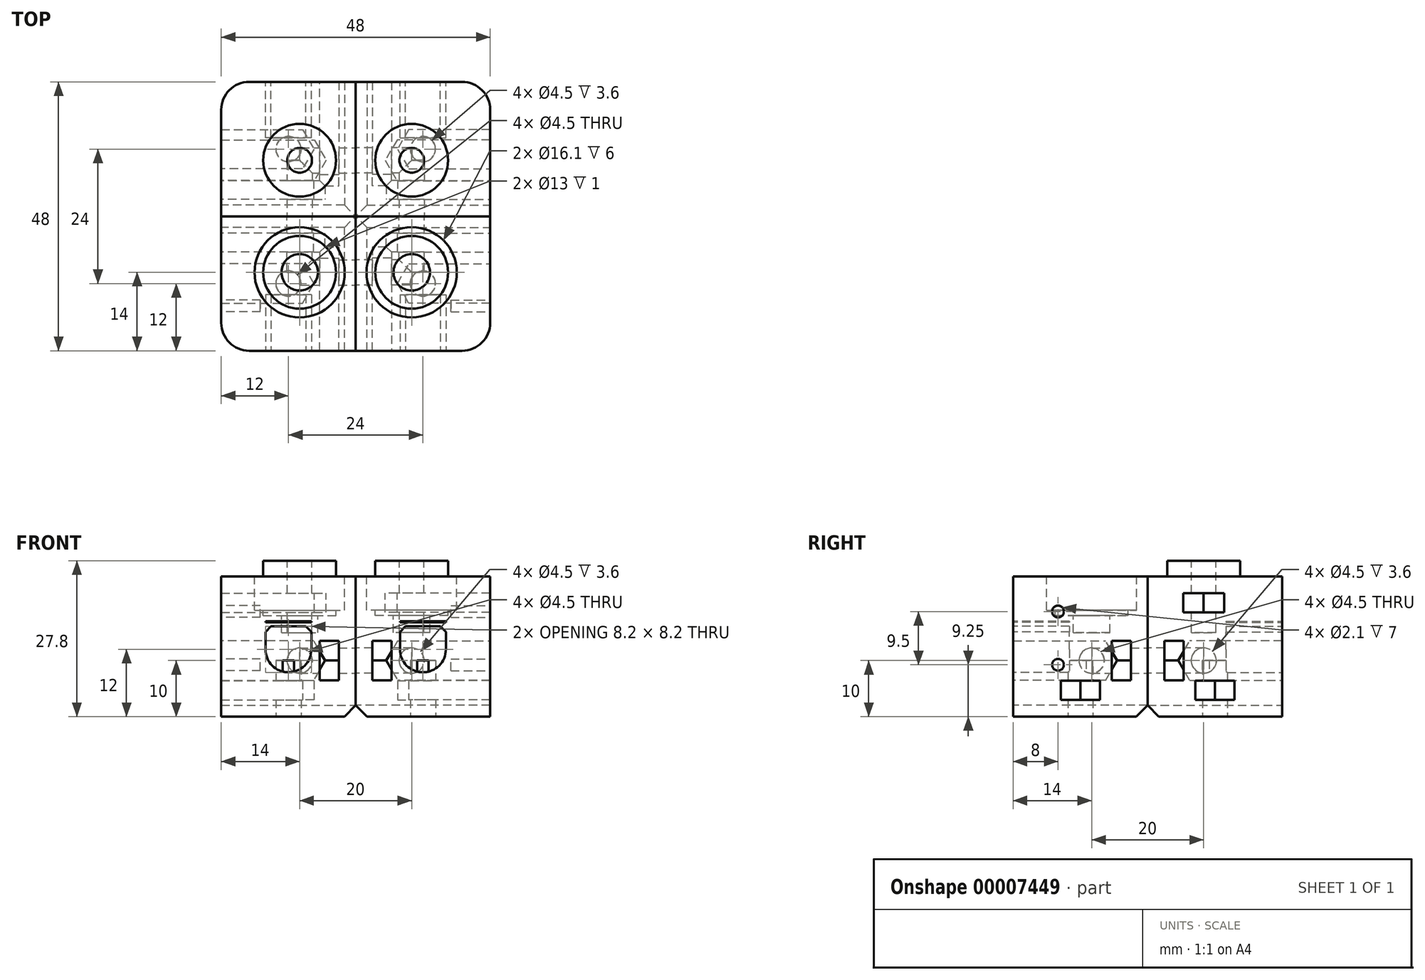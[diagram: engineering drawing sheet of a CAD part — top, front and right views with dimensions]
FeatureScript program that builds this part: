
annotation { "Feature Type Name" : "Feature", "Feature Type Description" : "" }
export const myFeature = defineFeature(function(context is Context, id is Id, definition is map)
    precondition{}
    {
        {
            var Q0;
            Q0=qCreatedBy(makeId("Top.planeOp"),FACE);
            var sketch = newSketch(context, id + "F0", { "sketchPlane" : qUnion([Q0])});
            skLineSegment(sketch, "E0.bottom", {"start": v(0, 0) * mm, "end": v(24, 0) * mm});
            skLineSegment(sketch, "E0.top", {"start": v(0, -24) * mm, "end": v(24, -24) * mm});
            skLineSegment(sketch, "E0.left", {"start": v(0, 0) * mm, "end": v(0, -24) * mm});
            skLineSegment(sketch, "E0.right", {"start": v(24, 0) * mm, "end": v(24, -24) * mm});
            skCircle(sketch, "E1", {"center": v(12, -12) * mm, "radius": 2.25 * mm});
            skLineSegment(sketch, "E2.3", {"start": v(9.48, -15.5) * mm, "end": v(7.46, -12) * mm});
            skLineSegment(sketch, "E2.4", {"start": v(7.46, -12) * mm, "end": v(9.48, -8.5) * mm});
            skLineSegment(sketch, "E3", {"start": v(24, -8.5) * mm, "end": v(24, -15.5) * mm});
            skLineSegment(sketch, "E4", {"start": v(9.48, -8.5) * mm, "end": v(24, -8.5) * mm});
            skLineSegment(sketch, "E5", {"start": v(24, -15.5) * mm, "end": v(9.48, -15.5) * mm});
            skLineSegment(sketch, "E6", {"start": v(8.47, -13.75) * mm, "end": v(11.5, -12) * mm, "construction": true});
            skLineSegment(sketch, "E7", {"start": v(11.5, -12) * mm, "end": v(12, -12) * mm, "construction": true});
            skLineSegment(sketch, "E8", {"start": v(7.46, -12) * mm, "end": v(11.5, -12) * mm, "construction": true});
            skSolve(sketch);
        }
        {
            var Q0;
            Q0 = qSketchRegion(id + "F0", true);
            var Q1;
            Q1=makeQuery(id+"F0.imprint","IMPRINT",FACE,{"disambiguationData":[TD([[makeQuery(id+"F0.imprint","IMPRINT",EDGE,{"derivedFrom":sQuery(id+"F0.wireOp",EDGE,"E1")}),-1.0]])]});
            var Q2;
            Q2=makeQuery(id+"F0.imprint","IMPRINT",FACE,{"disambiguationData":[TD([[makeQuery(id+"F0.imprint","IMPRINT",EDGE,{"derivedFrom":sQuery(id+"F0.wireOp",EDGE,"E1")}),1.0]])]});
            extrude(context, id + "F1", {"entities" : qUnion([Q0, Q1, Q2]), "depth" : 25 * mm});
        }
        {
            var Q0;
            Q0=makeQuery(id+"F0.imprint","IMPRINT",FACE,{"disambiguationData":[TD([[makeQuery(id+"F0.imprint","IMPRINT",EDGE,{"derivedFrom":sQuery(id+"F0.wireOp",EDGE,"E1")}),1.0]])]});
            extrude(context, id + "F2", {"entities" : qUnion([Q0]), "operationType" : NewBodyOperationType.REMOVE, "depth" : 10 * mm});
        }
        {
            var Q0;
            Q0=makeQuery(id+"F0.imprint","IMPRINT",FACE,{"disambiguationData":[TD([[makeQuery(id+"F0.imprint","IMPRINT",EDGE,{"derivedFrom":sQuery(id+"F0.wireOp",EDGE,"E2.0")}),1.0]])]});
            var Q1;
            Q1=makeQuery(id+"F0.imprint","IMPRINT",FACE,{"disambiguationData":[TD([[makeQuery(id+"F0.imprint","IMPRINT",EDGE,{"derivedFrom":sQuery(id+"F0.wireOp",EDGE,"E1")}),-1.0]])]});
            extrude(context, id + "F3", {"entities" : qUnion([Q0, Q1]), "operationType" : NewBodyOperationType.REMOVE, "depth" : 3 * mm + 3.4 * mm});
        }
        {
            var Q0;
            Q0=makeQuery(id+"F0.imprint","IMPRINT",FACE,{"disambiguationData":[TD([[makeQuery(id+"F0.imprint","IMPRINT",EDGE,{"derivedFrom":sQuery(id+"F0.wireOp",EDGE,"E1")}),-1.0]])]});
            var Q1;
            Q1=makeQuery(id+"F0.imprint","IMPRINT",FACE,{"disambiguationData":[TD([[makeQuery(id+"F0.imprint","IMPRINT",EDGE,{"derivedFrom":sQuery(id+"F0.wireOp",EDGE,"E2.0")}),1.0]])]});
            extrude(context, id + "F4", {"entities" : qUnion([Q0, Q1]), "operationType" : NewBodyOperationType.ADD, "depth" : 3 * mm});
        }
        {
            var Q0;
            Q0=makeQuery(id+"F1.opExtrude","SWEPT_FACE",FACE,{"disambiguationData":[OSD([sQuery(id+"F0.wireOp",EDGE,"E0.top")])]});
            var sketch = newSketch(context, id + "F5", { "sketchPlane" : qUnion([Q0])});
            skCircle(sketch, "E9", {"center": v(12, 12) * mm, "radius": 4 * mm});
            skLineSegment(sketch, "E10", {"start": v(8.72, 14.3) * mm, "end": v(10.76, 17.2) * mm});
            skLineSegment(sketch, "E11", {"start": v(10.76, 17.2) * mm, "end": v(13.24, 17.2) * mm});
            skLineSegment(sketch, "E12", {"start": v(13.24, 17.2) * mm, "end": v(15.28, 14.3) * mm});
            skSolve(sketch);
        }
        {
            var Q0;
            {var subQ1=sQuery(id+"F5.wireOp",EDGE,"E10");Q0=makeQuery(id+"F5.imprint","IMPRINT",FACE,{"disambiguationData":[TD([[makeQuery(id+"F5.imprint","IMPRINT",EDGE,{"derivedFrom":subQ1}),1.0]])]});}
            var sketch = newSketch(context, id + "F6", { "sketchPlane" : qUnion([Q0])});
            skCircle(sketch, "E13", {"center": v(12, 12) * mm, "radius": 4.1 * mm});
            skLineSegment(sketch, "E14", {"start": v(16.1, 12) * mm, "end": v(16.1, 16.1) * mm, "construction": true});
            skLineSegment(sketch, "E15", {"start": v(16.1, 16.1) * mm, "end": v(7.9, 16.1) * mm});
            skLineSegment(sketch, "E16", {"start": v(7.9, 16.1) * mm, "end": v(7.9, 12) * mm, "construction": true});
            skLineSegment(sketch, "E17", {"start": v(7.9, 16.1) * mm, "end": v(7.9, 17) * mm, "construction": true});
            skLineSegment(sketch, "E18", {"start": v(7.9, 17) * mm, "end": v(7.9, 16.8) * mm});
            skLineSegment(sketch, "E19", {"start": v(7.9, 16.8) * mm, "end": v(16.1, 16.8) * mm});
            skLineSegment(sketch, "E20", {"start": v(16.1, 16.8) * mm, "end": v(16.1, 17) * mm});
            skLineSegment(sketch, "E21", {"start": v(16.1, 17) * mm, "end": v(7.9, 17) * mm});
            skLineSegment(sketch, "E22", {"start": v(15.1, 16.1) * mm, "end": v(16.1, 15.1) * mm});
            skLineSegment(sketch, "E23", {"start": v(16.1, 15.1) * mm, "end": v(16.1, 12) * mm});
            skLineSegment(sketch, "E24", {"start": v(7.9, 12) * mm, "end": v(7.9, 15.1) * mm});
            skLineSegment(sketch, "E25", {"start": v(7.9, 15.1) * mm, "end": v(8.9, 16.1) * mm});
            skSolve(sketch);
        }
        {
            var Q0;
            Q0 = qSketchRegion(id + "F6", true);
            extrude(context, id + "F7", {"entities" : qUnion([Q0]), "operationType" : NewBodyOperationType.REMOVE, "oppositeDirection" : true, "depth" : 10 * mm});
        }
        {
            var Q0;
            Q0=makeQuery(id+"F1.opExtrude","SWEPT_FACE",FACE,{"disambiguationData":[OSD([sQuery(id+"F0.wireOp",EDGE,"E0.left")])]});
            var sketch = newSketch(context, id + "F8", { "sketchPlane" : qUnion([Q0])});
            skCircle(sketch, "E26", {"center": v(10, 10) * mm, "radius": 2.25 * mm});
            skLineSegment(sketch, "E27.3", {"start": v(7.48, 6.5) * mm, "end": v(5.46, 10) * mm});
            skLineSegment(sketch, "E27.4", {"start": v(5.46, 10) * mm, "end": v(7.48, 13.5) * mm});
            skLineSegment(sketch, "E28", {"start": v(24, 6.5) * mm, "end": v(24, 13.5) * mm});
            skLineSegment(sketch, "E29", {"start": v(24, 13.5) * mm, "end": v(7.48, 13.5) * mm});
            skLineSegment(sketch, "E30", {"start": v(7.48, 6.5) * mm, "end": v(24, 6.5) * mm});
            skLineSegment(sketch, "E31", {"start": v(10, 13.5) * mm, "end": v(10, 6.5) * mm, "construction": true});
            skLineSegment(sketch, "E32", {"start": v(6.47, 11.75) * mm, "end": v(9.5, 10) * mm, "construction": true});
            skLineSegment(sketch, "E33", {"start": v(9.5, 10) * mm, "end": v(10, 10) * mm, "construction": true});
            skSolve(sketch);
        }
        {
            var Q0;
            Q0=makeQuery(id+"F8.imprint","IMPRINT",FACE,{"disambiguationData":[TD([[makeQuery(id+"F8.imprint","IMPRINT",EDGE,{"derivedFrom":sQuery(id+"F8.wireOp",EDGE,"E26")}),1.0]])]});
            extrude(context, id + "F9", {"entities" : qUnion([Q0]), "operationType" : NewBodyOperationType.REMOVE, "oppositeDirection" : true, "depth" : 10 * mm});
        }
        {
            var Q0;
            Q0=makeQuery(id+"F8.imprint","IMPRINT",FACE,{"disambiguationData":[TD([[makeQuery(id+"F8.imprint","IMPRINT",EDGE,{"derivedFrom":sQuery(id+"F8.wireOp",EDGE,"E26")}),-1.0]])]});
            var Q1;
            Q1=makeQuery(id+"F8.imprint","IMPRINT",FACE,{"disambiguationData":[TD([[makeQuery(id+"F8.imprint","IMPRINT",EDGE,{"derivedFrom":sQuery(id+"F8.wireOp",EDGE,"E27.0")}),1.0]])]});
            extrude(context, id + "F10", {"entities" : qUnion([Q0, Q1]), "operationType" : NewBodyOperationType.REMOVE, "oppositeDirection" : true, "depth" : 3 * mm + 3.4 * mm});
        }
        {
            var Q0;
            Q0=makeQuery(id+"F8.imprint","IMPRINT",FACE,{"disambiguationData":[TD([[makeQuery(id+"F8.imprint","IMPRINT",EDGE,{"derivedFrom":sQuery(id+"F8.wireOp",EDGE,"E26")}),-1.0]])]});
            var Q1;
            Q1=makeQuery(id+"F8.imprint","IMPRINT",FACE,{"disambiguationData":[TD([[makeQuery(id+"F8.imprint","IMPRINT",EDGE,{"derivedFrom":sQuery(id+"F8.wireOp",EDGE,"E27.0")}),1.0]])]});
            extrude(context, id + "F11", {"entities" : qUnion([Q0, Q1]), "operationType" : NewBodyOperationType.ADD, "oppositeDirection" : true, "depth" : 3 * mm});
        }
        {
            var Q0;
            Q0=makeQuery(id+"F1.opExtrude","SWEPT_FACE",FACE,{"disambiguationData":[OSD([sQuery(id+"F0.wireOp",EDGE,"E0.bottom")])]});
            var sketch = newSketch(context, id + "F12", { "sketchPlane" : qUnion([Q0])});
            skCircle(sketch, "E34", {"center": v(-10, 10) * mm, "radius": 2.25 * mm});
            skLineSegment(sketch, "E35.0", {"start": v(-7.48, 13.5) * mm, "end": v(-5.46, 10) * mm});
            skLineSegment(sketch, "E35.1", {"start": v(-5.46, 10) * mm, "end": v(-7.48, 6.5) * mm});
            skPoint(sketch, "E35.0.midPoint", {"position": v(-6.47, 11.75) * mm});
            skLineSegment(sketch, "E36", {"start": v(-24, 13.5) * mm, "end": v(-24, 6.5) * mm});
            skLineSegment(sketch, "E37", {"start": v(-7.48, 13.5) * mm, "end": v(-24, 13.5) * mm});
            skLineSegment(sketch, "E38", {"start": v(-24, 6.5) * mm, "end": v(-7.48, 6.5) * mm});
            skLineSegment(sketch, "E39", {"start": v(-10, 13.5) * mm, "end": v(-10, 6.5) * mm, "construction": true});
            skLineSegment(sketch, "E40", {"start": v(-6.47, 11.75) * mm, "end": v(-9.5, 10) * mm});
            skLineSegment(sketch, "E41", {"start": v(-9.5, 10) * mm, "end": v(-10, 10) * mm});
            skSolve(sketch);
        }
        {
            var Q0;
            Q0=makeQuery(id+"F12.imprint","IMPRINT",FACE,{"disambiguationData":[TD([[makeQuery(id+"F12.imprint","IMPRINT",EDGE,{"derivedFrom":sQuery(id+"F12.wireOp",EDGE,"E34")}),1.0]])]});
            extrude(context, id + "F13", {"entities" : qUnion([Q0]), "operationType" : NewBodyOperationType.REMOVE, "oppositeDirection" : true, "depth" : 10 * mm});
        }
        {
            var Q0;
            Q0=makeQuery(id+"F12.imprint","IMPRINT",FACE,{"disambiguationData":[TD([[makeQuery(id+"F12.imprint","IMPRINT",EDGE,{"derivedFrom":sQuery(id+"F12.wireOp",EDGE,"E35.3")}),1.0]])]});
            var Q1;
            Q1=makeQuery(id+"F12.imprint","IMPRINT",FACE,{"disambiguationData":[TD([[makeQuery(id+"F12.imprint","IMPRINT",EDGE,{"derivedFrom":sQuery(id+"F12.wireOp",EDGE,"E34")}),-1.0]])]});
            extrude(context, id + "F14", {"entities" : qUnion([Q0, Q1]), "operationType" : NewBodyOperationType.REMOVE, "oppositeDirection" : true, "depth" : 3 * mm + 3.4 * mm});
        }
        {
            var Q0;
            Q0=makeQuery(id+"F12.imprint","IMPRINT",FACE,{"disambiguationData":[TD([[makeQuery(id+"F12.imprint","IMPRINT",EDGE,{"derivedFrom":sQuery(id+"F12.wireOp",EDGE,"E35.3")}),1.0]])]});
            var Q1;
            Q1=makeQuery(id+"F12.imprint","IMPRINT",FACE,{"disambiguationData":[TD([[makeQuery(id+"F12.imprint","IMPRINT",EDGE,{"derivedFrom":sQuery(id+"F12.wireOp",EDGE,"E34")}),-1.0]])]});
            extrude(context, id + "F15", {"entities" : qUnion([Q0, Q1]), "operationType" : NewBodyOperationType.ADD, "oppositeDirection" : true, "depth" : 3 * mm});
        }
        {
            var Q0;
            Q0=makeQuery(id+"F1.opExtrude","SWEPT_EDGE",EDGE,{"disambiguationData":[OSD([sQuery(id+"F0.wireOp",EDGE,"E0.top"),sQuery(id+"F0.wireOp",EDGE,"E0.right")])]});
            fillet(context, id + "F16", {"entities" : qUnion([Q0]), "radius" : 5 * mm, "tangentPropagation" : true, "allowEdgeOverflow" : false});
        }
        {
            var Q0;
            Q0=makeQuery(id+"F1.opExtrude","CAP_EDGE",EDGE,{"disambiguationData":[OSD([sQuery(id+"F0.wireOp",EDGE,"E0.left")])],"isStart":true});
            var Q1;
            Q1=makeQuery(id+"F1.opExtrude","CAP_EDGE",EDGE,{"disambiguationData":[OSD([sQuery(id+"F0.wireOp",EDGE,"E0.bottom")])],"isStart":true});
            chamfer(context, id + "F17", {"entities" : qUnion([Q0, Q1]), "width" : 2 * mm, "tangentPropagation" : true});
        }
        {
            var Q0;
            Q0=makeQuery(id+"F1.opExtrude","SWEPT_BODY",BODY,{"disambiguationData":[OSD([sQuery(id+"F0.wireOp",EDGE,"E0.bottom"),sQuery(id+"F0.wireOp",EDGE,"E0.top"),sQuery(id+"F0.wireOp",EDGE,"E0.left"),sQuery(id+"F0.wireOp",EDGE,"E0.right"),sQuery(id+"F0.wireOp",EDGE,"E3")])]});
            var Q1;
            Q1=qCreatedBy(makeId("Front.planeOp"),FACE);
            mirror(context, id + "F18", {"entities" : qUnion([Q0]), "mirrorPlane" : qUnion([Q1])});
        }
        {
            var Q0;
            Q0=makeQuery(id+"F18.opPattern","COPY",FACE,{"derivedFrom":makeQuery(id+"F1.opExtrude","CAP_FACE",FACE,{"disambiguationData":[OSD([sQuery(id+"F0.wireOp",EDGE,"E0.bottom"),sQuery(id+"F0.wireOp",EDGE,"E0.top"),sQuery(id+"F0.wireOp",EDGE,"E0.left"),sQuery(id+"F0.wireOp",EDGE,"E0.right"),sQuery(id+"F0.wireOp",EDGE,"E3")])],"isStart":false}),"instanceName":"1"});
            var sketch = newSketch(context, id + "F19", { "sketchPlane" : qUnion([Q0])});
            skCircle(sketch, "E42", {"center": v(10, 10) * mm, "radius": 2.2 * mm});
            skCircle(sketch, "E43", {"center": v(10, 10) * mm, "radius": 6.5 * mm});
            skLineSegment(sketch, "E44", {"start": v(24, 13.65) * mm, "end": v(24, 6.35) * mm});
            skLineSegment(sketch, "E45", {"start": v(24, 13.65) * mm, "end": v(7.4, 13.65) * mm});
            skLineSegment(sketch, "E46", {"start": v(7.4, 13.65) * mm, "end": v(5.29, 10) * mm});
            skLineSegment(sketch, "E47", {"start": v(5.29, 10) * mm, "end": v(7.4, 6.35) * mm});
            skLineSegment(sketch, "E48", {"start": v(7.4, 6.35) * mm, "end": v(24, 6.35) * mm});
            skLineSegment(sketch, "E49", {"start": v(6.34, 11.83) * mm, "end": v(9.5, 10) * mm, "construction": true});
            skLineSegment(sketch, "E50", {"start": v(9.5, 10) * mm, "end": v(10, 10) * mm, "construction": true});
            skLineSegment(sketch, "E51", {"start": v(5.29, 10) * mm, "end": v(9.5, 10) * mm, "construction": true});
            skSolve(sketch);
        }
        {
            var Q0;
            Q0=makeQuery(id+"F19.imprint","IMPRINT",FACE,{"disambiguationData":[TD([[makeQuery(id+"F19.imprint","IMPRINT",EDGE,{"derivedFrom":sQuery(id+"F19.wireOp",EDGE,"E42")}),1.0]])]});
            extrude(context, id + "F20", {"entities" : qUnion([Q0]), "operationType" : NewBodyOperationType.REMOVE, "oppositeDirection" : true, "depth" : 10 * mm});
        }
        {
            var Q0;
            {var subQ6=sQuery(id+"F19.wireOp",EDGE,"3c2f8247-9d55-409e-9478-93798bc3c1df.1");Q0=makeQuery(id+"F19.imprint","IMPRINT",FACE,{"disambiguationData":[TD([[makeQuery(id+"F19.imprint","IMPRINT",EDGE,{"derivedFrom":subQ6}),1.0]])]});}
            var Q1;
            {var subQ4=sQuery(id+"F19.wireOp",EDGE,"E44");Q1=makeQuery(id+"F19.imprint","IMPRINT",FACE,{"disambiguationData":[TD([[makeQuery(id+"F19.imprint","IMPRINT",EDGE,{"derivedFrom":subQ4}),1.0]])]});}
            var Q2;
            Q2=makeQuery(id+"F19.imprint","IMPRINT",FACE,{"disambiguationData":[TD([[makeQuery(id+"F19.imprint","IMPRINT",EDGE,{"derivedFrom":sQuery(id+"F19.wireOp",EDGE,"E42")}),-1.0]])]});
            extrude(context, id + "F21", {"entities" : qUnion([Q0, Q1, Q2]), "operationType" : NewBodyOperationType.REMOVE, "oppositeDirection" : true, "depth" : 3 * mm + 3.4 * mm});
        }
        {
            var Q0;
            Q0=makeQuery(id+"F19.imprint","IMPRINT",FACE,{"disambiguationData":[TD([[makeQuery(id+"F19.imprint","IMPRINT",EDGE,{"derivedFrom":sQuery(id+"F19.wireOp",EDGE,"E42")}),-1.0]])]});
            var Q1;
            {var subQ4=sQuery(id+"F19.wireOp",EDGE,"E44");Q1=makeQuery(id+"F19.imprint","IMPRINT",FACE,{"disambiguationData":[TD([[makeQuery(id+"F19.imprint","IMPRINT",EDGE,{"derivedFrom":subQ4}),1.0]])]});}
            var Q2;
            {var subQ6=sQuery(id+"F19.wireOp",EDGE,"3c2f8247-9d55-409e-9478-93798bc3c1df.1");Q2=makeQuery(id+"F19.imprint","IMPRINT",FACE,{"disambiguationData":[TD([[makeQuery(id+"F19.imprint","IMPRINT",EDGE,{"derivedFrom":subQ6}),1.0]])]});}
            extrude(context, id + "F22", {"entities" : qUnion([Q0, Q1, Q2]), "operationType" : NewBodyOperationType.ADD, "oppositeDirection" : true, "depth" : 3 * mm});
        }
        {
            var Q0;
            {var subQ4=sQuery(id+"F19.wireOp",EDGE,"E46");Q0=makeQuery(id+"F19.imprint","IMPRINT",FACE,{"disambiguationData":[TD([[makeQuery(id+"F19.imprint","IMPRINT",EDGE,{"derivedFrom":subQ4}),-1.0]])]});}
            var Q1;
            Q1=makeQuery(id+"F19.imprint","IMPRINT",FACE,{"disambiguationData":[TD([[makeQuery(id+"F19.imprint","IMPRINT",EDGE,{"derivedFrom":sQuery(id+"F19.wireOp",EDGE,"E42")}),-1.0]])]});
            extrude(context, id + "F23", {"entities" : qUnion([Q0, Q1]), "operationType" : NewBodyOperationType.ADD, "depth" : 16 * mm + 12 * mm - 25 * mm - .2 * mm});
        }
        {
            var Q0;
            Q0=makeQuery(id+"F1.opExtrude","CAP_FACE",FACE,{"disambiguationData":[OSD([sQuery(id+"F0.wireOp",EDGE,"E0.bottom"),sQuery(id+"F0.wireOp",EDGE,"E0.top"),sQuery(id+"F0.wireOp",EDGE,"E0.left"),sQuery(id+"F0.wireOp",EDGE,"E0.right")])],"isStart":false});
            var sketch = newSketch(context, id + "F24", { "sketchPlane" : qUnion([Q0])});
            skCircle(sketch, "E52", {"center": v(10, -10) * mm, "radius": 3.25 * mm});
            skCircle(sketch, "E53", {"center": v(10, -10) * mm, "radius": 8.05 * mm});
            skCircle(sketch, "E54", {"center": v(10, -10) * mm, "radius": 6.5 * mm});
            skSolve(sketch);
        }
        {
            var Q0;
            Q0=makeQuery(id+"F24.imprint","IMPRINT",FACE,{"disambiguationData":[TD([[makeQuery(id+"F24.imprint","IMPRINT",EDGE,{"derivedFrom":sQuery(id+"F24.wireOp",EDGE,"E52")}),1.0]])]});
            extrude(context, id + "F25", {"entities" : qUnion([Q0]), "operationType" : NewBodyOperationType.REMOVE, "oppositeDirection" : true, "depth" : 10 * mm});
        }
        {
            var Q0;
            Q0=makeQuery(id+"F24.imprint","IMPRINT",FACE,{"disambiguationData":[TD([[makeQuery(id+"F24.imprint","IMPRINT",EDGE,{"derivedFrom":sQuery(id+"F24.wireOp",EDGE,"E52")}),-1.0]])]});
            var Q1;
            Q1=makeQuery(id+"F24.imprint","IMPRINT",FACE,{"disambiguationData":[TD([[makeQuery(id+"F24.imprint","IMPRINT",EDGE,{"derivedFrom":sQuery(id+"F24.wireOp",EDGE,"E53")}),1.0]])]});
            extrude(context, id + "F26", {"entities" : qUnion([Q0, Q1]), "operationType" : NewBodyOperationType.REMOVE, "oppositeDirection" : true, "depth" : 6 * mm});
        }
        {
            var Q0;
            Q0=makeQuery(id+"F24.imprint","IMPRINT",FACE,{"disambiguationData":[TD([[makeQuery(id+"F24.imprint","IMPRINT",EDGE,{"derivedFrom":sQuery(id+"F24.wireOp",EDGE,"E52")}),-1.0]])]});
            extrude(context, id + "F27", {"entities" : qUnion([Q0]), "operationType" : NewBodyOperationType.REMOVE, "oppositeDirection" : true, "depth" : 7 * mm});
        }
        {
            var Q0;
            {var subQ0=sQuery(id+"F0.wireOp",EDGE,"E3");Q0=makeQuery(id+"F15.boolean.opBoolean","MERGE",FACE,{"derivedFrom":[makeQuery(id+"F4.boolean.opBoolean","MERGE",FACE,{"derivedFrom":[makeQuery(id+"F1.opExtrude","SWEPT_FACE",FACE,{"disambiguationData":[OSD([sQuery(id+"F0.wireOp",EDGE,"E0.right"),subQ0])]}),makeQuery(id+"F4.opExtrude","SWEPT_FACE",FACE,{"disambiguationData":[OSD([subQ0])]})]}),makeQuery(id+"F15.opExtrude","SWEPT_FACE",FACE,{"disambiguationData":[OSD([sQuery(id+"F12.wireOp",EDGE,"E36")])]})]});}
            var sketch = newSketch(context, id + "F28", { "sketchPlane" : qUnion([Q0])});
            skLineSegment(sketch, "E55", {"start": v(-16, 18.75) * mm, "end": v(-16, 9.25) * mm, "construction": true});
            skCircle(sketch, "E56", {"center": v(-16, 18.75) * mm, "radius": 1.05 * mm});
            skCircle(sketch, "E57", {"center": v(-16, 9.25) * mm, "radius": 1.05 * mm});
            skPoint(sketch, "E58", {"position": v(-16, 14) * mm});
            skSolve(sketch);
        }
        {
            var Q0;
            Q0 = qSketchRegion(id + "F28", true);
            extrude(context, id + "F29", {"entities" : qUnion([Q0]), "operationType" : NewBodyOperationType.REMOVE, "oppositeDirection" : true, "depth" : 7 * mm});
        }
        {
            var Q0;
            Q0=makeQuery(id+"F1.opExtrude","SWEPT_BODY",BODY,{"disambiguationData":[OSD([sQuery(id+"F0.wireOp",EDGE,"E0.bottom"),sQuery(id+"F0.wireOp",EDGE,"E0.top"),sQuery(id+"F0.wireOp",EDGE,"E0.left"),sQuery(id+"F0.wireOp",EDGE,"E0.right"),sQuery(id+"F0.wireOp",EDGE,"E3")])]});
            var Q1;
            Q1=qCreatedBy(makeId("Right.planeOp"),FACE);
            mirror(context, id + "F30", {"entities" : qUnion([Q0]), "mirrorPlane" : qUnion([Q1])});
        }
        {
            var Q0;
            Q0=makeQuery(id+"F18.opPattern","COPY",BODY,{"derivedFrom":makeQuery(id+"F1.opExtrude","SWEPT_BODY",BODY,{"disambiguationData":[OSD([sQuery(id+"F0.wireOp",EDGE,"E0.bottom"),sQuery(id+"F0.wireOp",EDGE,"E0.top"),sQuery(id+"F0.wireOp",EDGE,"E0.left"),sQuery(id+"F0.wireOp",EDGE,"E0.right"),sQuery(id+"F0.wireOp",EDGE,"E3")])]}),"instanceName":"1"});
            var Q1;
            Q1=qCreatedBy(makeId("Right.planeOp"),FACE);
            mirror(context, id + "F31", {"entities" : qUnion([Q0]), "mirrorPlane" : qUnion([Q1])});
        }
    });
